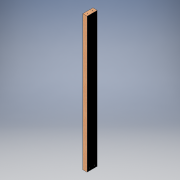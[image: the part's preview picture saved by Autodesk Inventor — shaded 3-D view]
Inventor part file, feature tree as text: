
AUTODESK INVENTOR PART (.ipt)
format: ipt  version: 2016 (Build 200138000, 138)  size: 122,368 bytes
history: native  units: in
note: dims shown in document units (in); Inventor stores cm internally (conversion verified against a paired STEP export)
features: extrude x3, sketch x3
ambient origin geometry x8: Origin, YZ Plane, XZ Plane, XY Plane, X Axis, Y Axis, Z Axis, Center Point
bodies: Solid1 (feature_tree)
feature tree (6):
  extrude  "Wood"  Depth=3.5in
  extrude  "Extrusion4"  Depth=46.5in
  extrude  "Extrusion5"  Depth=1.5in
  sketch  "Sketch1"  dims[d0=1.5in d1=3.5in]
  sketch  "Sketch4"  dims[d2=46.5in d3=0.0in d11=0.1875in]
  sketch  "Sketch5"  dims[d12=1.5in d13=0.0in d14=1.5in d15=0.1875in d16=1.5in d17=0.0in]
